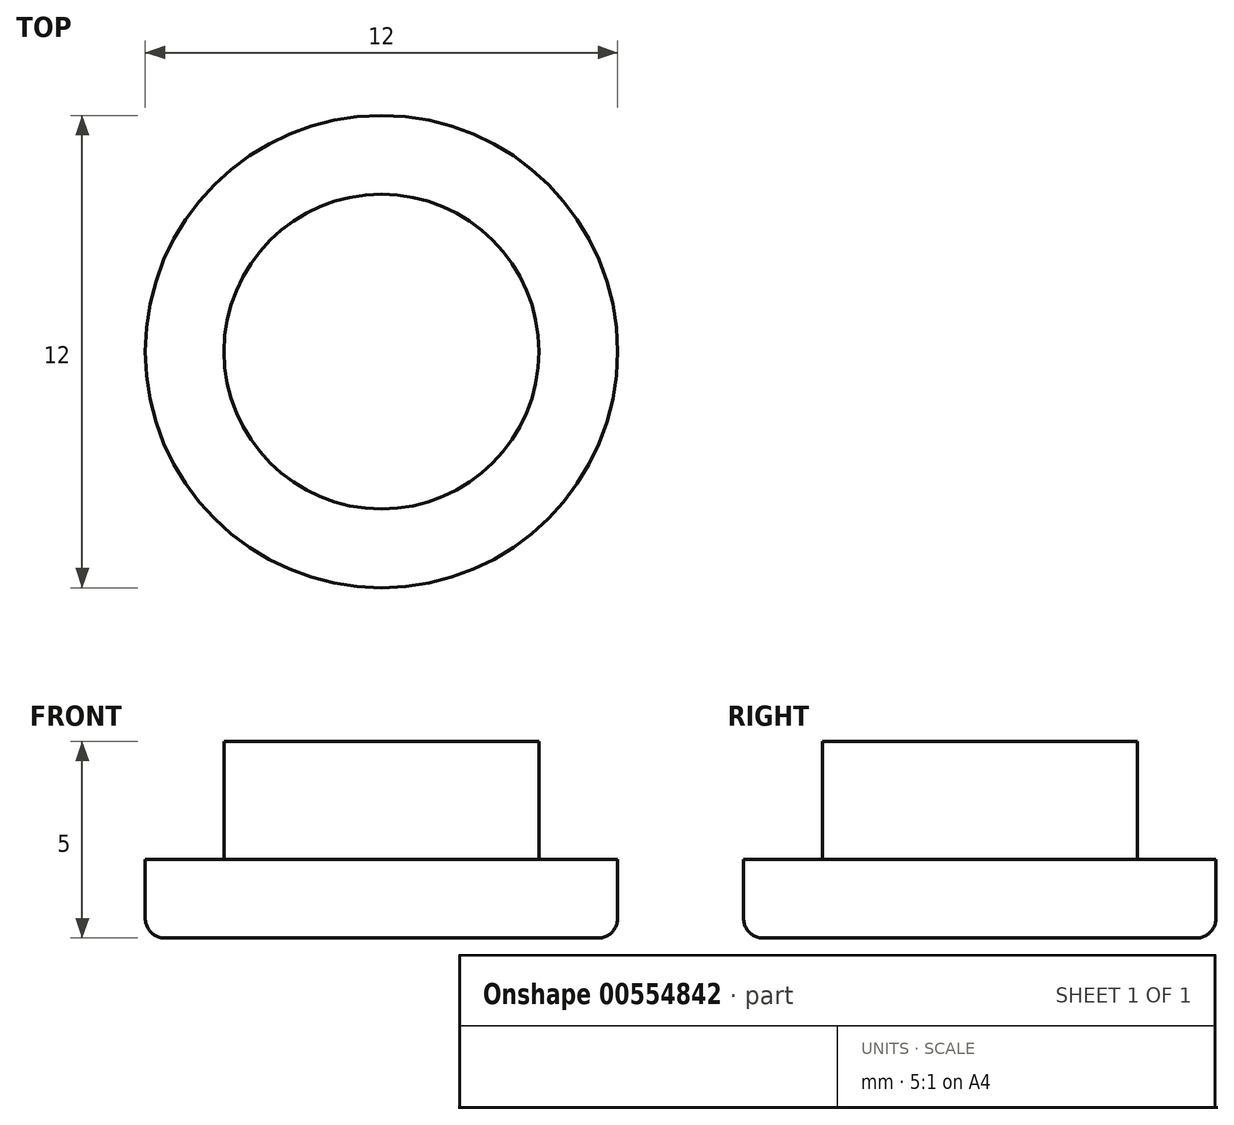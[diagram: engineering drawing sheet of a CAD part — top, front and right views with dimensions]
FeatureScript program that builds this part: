
annotation { "Feature Type Name" : "Feature", "Feature Type Description" : "" }
export const myFeature = defineFeature(function(context is Context, id is Id, definition is map)
    precondition{}
    {
        {
            var Q0;
            Q0=qCreatedBy(makeId("Top.planeOp"),FACE);
            var sketch = newSketch(context, id + "F0", { "sketchPlane" : qUnion([Q0])});
            skCircle(sketch, "E0", {"center": v(0, 0) * mm, "radius": 6 * mm});
            skSolve(sketch);
        }
        {
            var Q0;
            Q0 = qSketchRegion(id + "F0", true);
            extrude(context, id + "F1", {"entities" : qUnion([Q0]), "depth" : 2 * mm, "offsetDistance" : 25 * mm});
        }
        {
            var Q0;
            Q0=qCreatedBy(makeId("Top.planeOp"),FACE);
            var sketch = newSketch(context, id + "F2", { "sketchPlane" : qUnion([Q0])});
            skCircle(sketch, "E1", {"center": v(0, 0) * mm, "radius": 4 * mm});
            skSolve(sketch);
        }
        {
            var Q0;
            Q0 = qSketchRegion(id + "F2", true);
            extrude(context, id + "F3", {"entities" : qUnion([Q0]), "operationType" : NewBodyOperationType.ADD, "depth" : 5 * mm, "offsetDistance" : 25 * mm});
        }
        {
            var Q0;
            Q0=makeQuery(id+"F1.opExtrude","CAP_EDGE",EDGE,{"disambiguationData":[OSD([sQuery(id+"F0.wireOp",EDGE,"E0")])],"isStart":true});
            fillet(context, id + "F4", {"entities" : qUnion([Q0]), "radius" : 0.5 * mm, "tangentPropagation" : true, "allowEdgeOverflow" : false});
        }
    });
